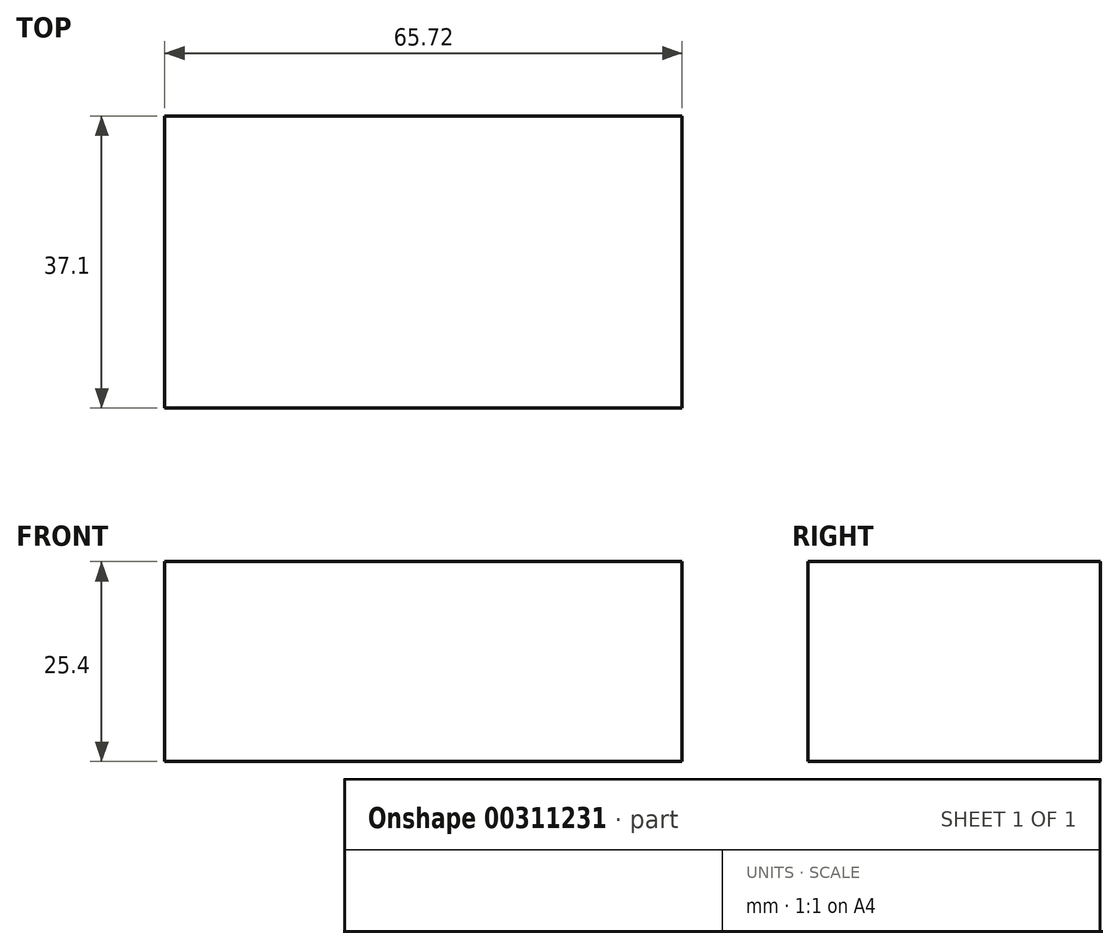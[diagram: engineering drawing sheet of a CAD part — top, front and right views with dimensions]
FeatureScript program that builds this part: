
annotation { "Feature Type Name" : "Feature", "Feature Type Description" : "" }
export const myFeature = defineFeature(function(context is Context, id is Id, definition is map)
    precondition{}
    {
        {
            var Q0;
            Q0=qCreatedBy(makeId("Top.planeOp"),FACE);
            var sketch = newSketch(context, id + "F0", { "sketchPlane" : qUnion([Q0])});
            skLineSegment(sketch, "E0.bottom", {"start": v(0, 0) * mm, "end": v(65.72, 0) * mm});
            skLineSegment(sketch, "E0.top", {"start": v(0, -37.1) * mm, "end": v(65.72, -37.1) * mm});
            skLineSegment(sketch, "E0.left", {"start": v(0, 0) * mm, "end": v(0, -37.1) * mm});
            skLineSegment(sketch, "E0.right", {"start": v(65.72, 0) * mm, "end": v(65.72, -37.1) * mm});
            skSolve(sketch);
        }
        {
            var Q0;
            Q0 = qSketchRegion(id + "F0", true);
            extrude(context, id + "F1", {"entities" : qUnion([Q0]), "depth" : 25.4 * mm});
        }
    });
